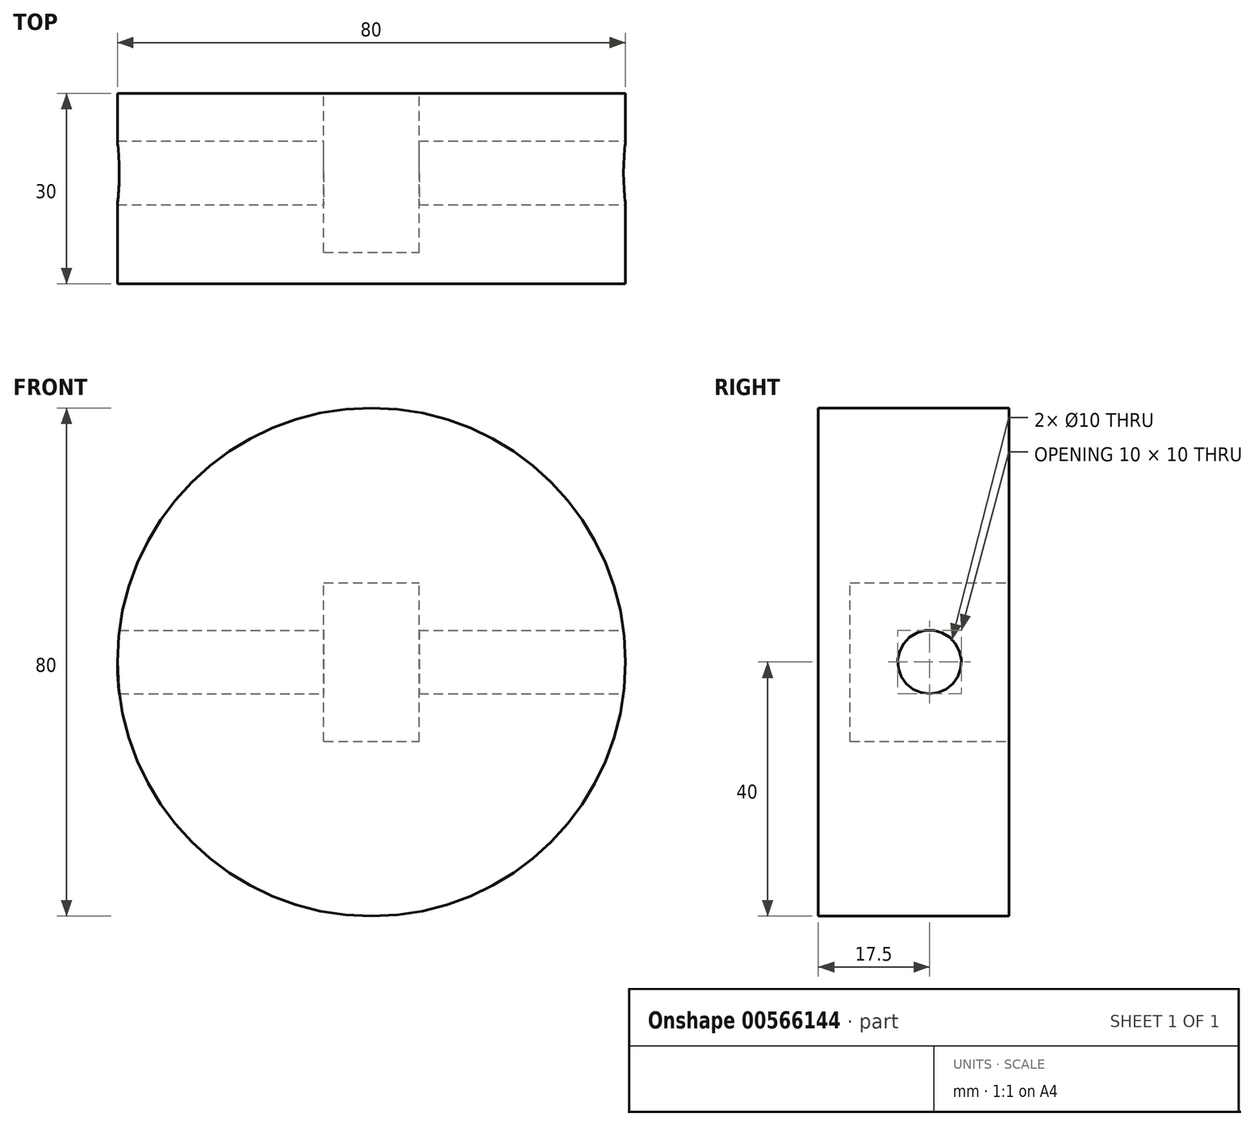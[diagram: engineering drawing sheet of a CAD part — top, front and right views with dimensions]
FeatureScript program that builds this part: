
annotation { "Feature Type Name" : "Feature", "Feature Type Description" : "" }
export const myFeature = defineFeature(function(context is Context, id is Id, definition is map)
    precondition{}
    {
        {
            var Q0;
            Q0=qCreatedBy(makeId("Front.planeOp"),FACE);
            var sketch = newSketch(context, id + "F0", { "sketchPlane" : qUnion([Q0])});
            skCircle(sketch, "E0", {"center": v(0, 0) * mm, "radius": 40 * mm});
            skSolve(sketch);
        }
        {
            var Q0;
            Q0=makeQuery(id+"F0.imprint","IMPRINT",FACE,{"disambiguationData":[TD([[makeQuery(id+"F0.imprint","IMPRINT",EDGE,{"derivedFrom":sQuery(id+"F0.wireOp",EDGE,"E0")}),1.0]])]});
            extrude(context, id + "F1", {"entities" : qUnion([Q0]), "oppositeDirection" : true, "depth" : 30 * mm, "offsetDistance" : 25.4 * mm});
        }
        {
            var Q0;
            Q0=makeQuery(id+"F1.opExtrude","CAP_FACE",FACE,{"disambiguationData":[OSD([sQuery(id+"F0.wireOp",EDGE,"E0")])],"isStart":false});
            var sketch = newSketch(context, id + "F2", { "sketchPlane" : qUnion([Q0])});
            skLineSegment(sketch, "E1.bottom", {"start": v(7.5, -12.5) * mm, "end": v(-7.5, -12.5) * mm});
            skLineSegment(sketch, "E1.top", {"start": v(7.5, 12.5) * mm, "end": v(-7.5, 12.5) * mm});
            skLineSegment(sketch, "E1.left", {"start": v(7.5, -12.5) * mm, "end": v(7.5, 12.5) * mm});
            skLineSegment(sketch, "E1.right", {"start": v(-7.5, -12.5) * mm, "end": v(-7.5, 12.5) * mm});
            skPoint(sketch, "E1.middle", {"position": v(0, 0) * mm});
            skSolve(sketch);
        }
        {
            var Q0;
            Q0 = qSketchRegion(id + "F2", true);
            extrude(context, id + "F3", {"entities" : qUnion([Q0]), "operationType" : NewBodyOperationType.REMOVE, "oppositeDirection" : true, "depth" : 25 * mm, "offsetDistance" : 25.4 * mm});
        }
        {
            var Q0;
            Q0=makeQuery(id+"F3.boolean.opBoolean","COPY",FACE,{"derivedFrom":makeQuery(id+"F3.opExtrude","SWEPT_FACE",FACE,{"disambiguationData":[OSD([sQuery(id+"F2.wireOp",EDGE,"E1.left")])]})});
            var sketch = newSketch(context, id + "F4", { "sketchPlane" : qUnion([Q0])});
            skCircle(sketch, "E2", {"center": v(17.5, 0) * mm, "radius": 5 * mm});
            skPoint(sketch, "E2.centerSnap0", {"position": v(17.5, -12.5) * mm});
            skSolve(sketch);
        }
        {
            var Q0;
            Q0 = qSketchRegion(id + "F4", true);
            extrude(context, id + "F5", {"entities" : qUnion([Q0]), "operationType" : NewBodyOperationType.REMOVE, "endBound" : BoundingType.SYMMETRIC, "oppositeDirection" : true, "depth" : 123.8 * mm, "offsetDistance" : 25.4 * mm});
        }
    });
